# Revit family: result
name_source: partatom
category: Specialty Equipment
revit_build: Autodesk Revit 2015 (Build: 20140903_1530(x64)
units: mm (PartAtom-declared; Revit-internal decimal feet)

## types (1)
- Default
    BIMobject category = Dispensers
    BIMobject category code = sanitary-dispensers
    BIMobject main category = Sanitary
    BIMobject main category code = sanitary
    Brand url = http://www.delabie.com
    Design country = Portugal
    Edition number = 1
    GTIN code = https://3456330163682
    IFC Classification = Furnishing Element
    Manufacturer country = France
    Manufacturer name = DELABIE
    Material main = Stainless steel
    OmniClass Code = 23-21 43 15 25
    OmniClass Description = Paper Towel Dispensers
    Product Guid = 5cc551ec-f614-4cda-b16e-04e3b195b49a
    Product SKU = 510715S
    Product data url = https://bimobject.com
    Product family = Sanitary
    Product group = Accessories
    Product name = 510715S Recessed combi paper towel dispenser/bin - 30L
    Product url = https://www.delabie.com
    QR code = http://bimobject.com
    Technical description = https://www.delabie.com
    UNSPSC Code = 301815
    Uniclass 2015 Code = Pr_40_70_22_75
    Uniclass 2015 Name = Sanitary towel dispensers

## geometry (parser evidence)
native form markers: Sweep x4
no freeform markers — native parametric forms only
